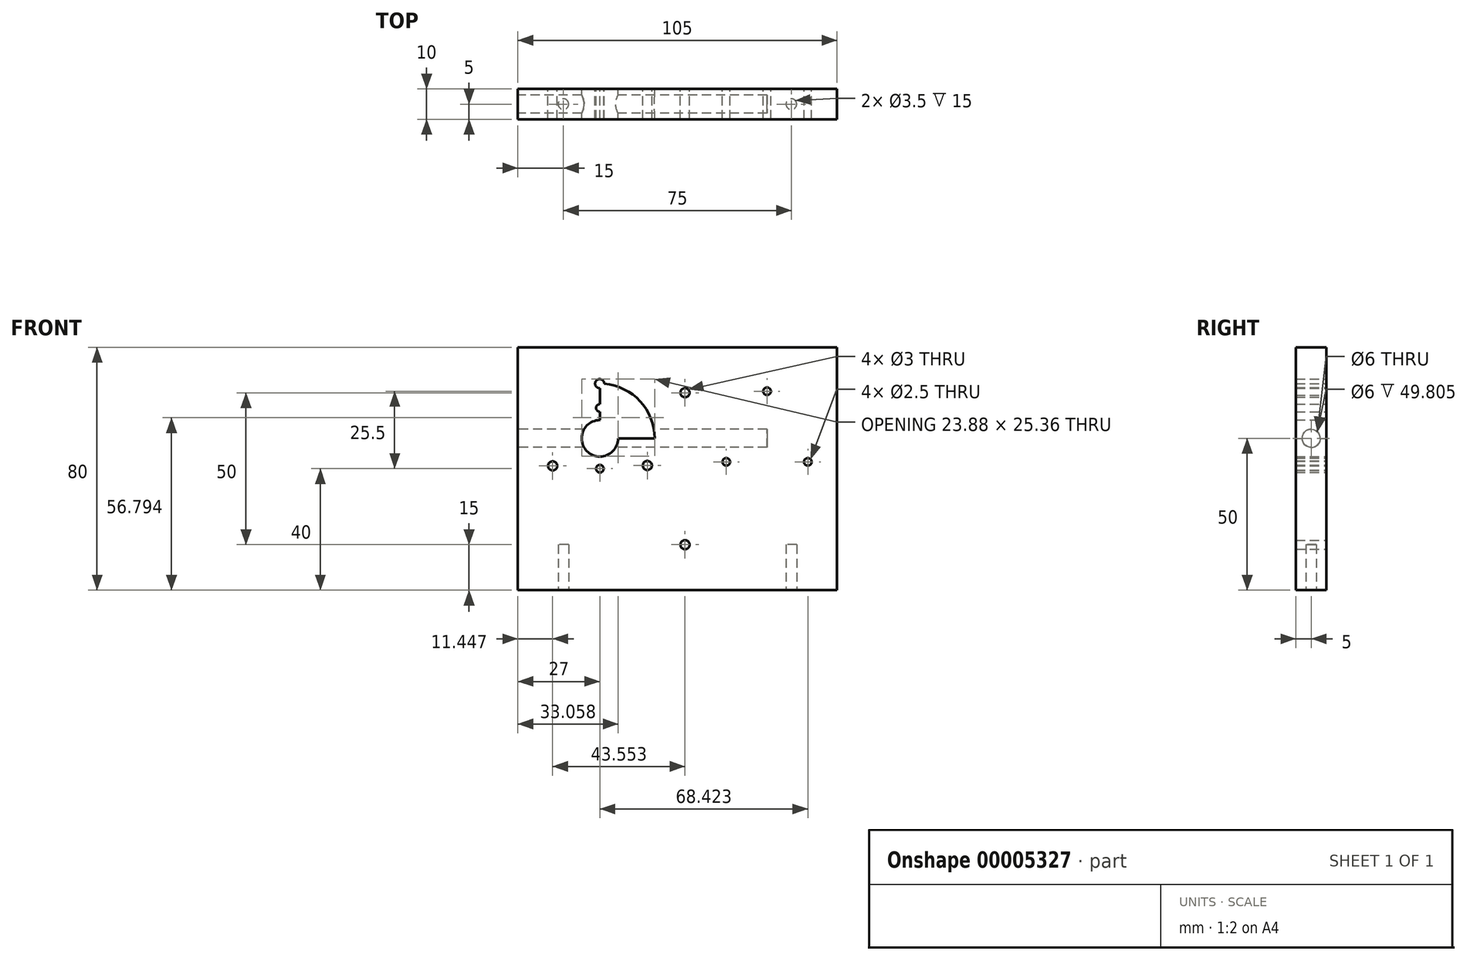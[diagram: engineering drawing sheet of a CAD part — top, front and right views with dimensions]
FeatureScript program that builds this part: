
annotation { "Feature Type Name" : "Feature", "Feature Type Description" : "" }
export const myFeature = defineFeature(function(context is Context, id is Id, definition is map)
    precondition{}
    {
        {
            var Q0;
            Q0=qCreatedBy(makeId("Front.planeOp"),FACE);
            var sketch = newSketch(context, id + "F0", { "sketchPlane" : qUnion([Q0])});
            skLineSegment(sketch, "E0.bottom", {"start": v(0, 0) * mm, "end": v(105, 0) * mm});
            skLineSegment(sketch, "E0.top", {"start": v(0, 80) * mm, "end": v(105, 80) * mm});
            skLineSegment(sketch, "E0.left", {"start": v(0, 0) * mm, "end": v(0, 80) * mm});
            skLineSegment(sketch, "E0.right", {"start": v(105, 0) * mm, "end": v(105, 80) * mm});
            skCircle(sketch, "E1", {"center": v(27, 50) * mm, "radius": 6 * mm});
            skCircle(sketch, "E2", {"center": v(27, 50) * mm, "radius": 18 * mm});
            skCircle(sketch, "E3", {"center": v(26.93, 68) * mm, "radius": 1.5 * mm});
            skCircle(sketch, "E4.1.0", {"center": v(11.45, 40.94) * mm, "radius": 1.5 * mm});
            skCircle(sketch, "E4.2.0", {"center": v(42.62, 41.06) * mm, "radius": 1.5 * mm});
            skLineSegment(sketch, "E5", {"start": v(27, 50) * mm, "end": v(27, 85.98) * mm});
            skLineSegment(sketch, "E6", {"start": v(27, 85.98) * mm, "end": v(27, 10.6) * mm});
            skCircle(sketch, "E7", {"center": v(27, 60) * mm, "radius": 1.25 * mm});
            skCircle(sketch, "E8", {"center": v(27, 40) * mm, "radius": 1.25 * mm});
            skLineSegment(sketch, "E9", {"start": v(27, 50) * mm, "end": v(101.77, 50) * mm});
            skCircle(sketch, "E10", {"center": v(82, 50) * mm, "radius": 15.5 * mm});
            skLineSegment(sketch, "E11", {"start": v(82, 50) * mm, "end": v(82, 71.42) * mm});
            skCircle(sketch, "E12", {"center": v(82, 65.5) * mm, "radius": 1.25 * mm});
            skCircle(sketch, "E13.1.0", {"center": v(95.42, 42.25) * mm, "radius": 1.25 * mm});
            skCircle(sketch, "E13.2.0", {"center": v(68.58, 42.25) * mm, "radius": 1.25 * mm});
            skLineSegment(sketch, "E13.anchor1", {"start": v(82, 50) * mm, "end": v(82, 65.5) * mm, "construction": true});
            skLineSegment(sketch, "E13.anchor2", {"start": v(82, 50) * mm, "end": v(68.58, 42.25) * mm, "construction": true});
            skCircle(sketch, "E14", {"center": v(55, 65) * mm, "radius": 1.5 * mm});
            skLineSegment(sketch, "E15", {"start": v(55, 65) * mm, "end": v(55, 3.51) * mm});
            skCircle(sketch, "E16", {"center": v(55, 15) * mm, "radius": 1.5 * mm});
            skSolve(sketch);
        }
        {
            var Q0;
            Q0=makeQuery(id+"F0.imprint","IMPRINT",FACE,{"disambiguationData":[TD([[makeQuery(id+"F0.imprint","IMPRINT",EDGE,{"derivedFrom":sQuery(id+"F0.wireOp",EDGE,"E0.bottom")}),1.0]])]});
            var Q1;
            {var subQ1=sQuery(id+"F0.wireOp",EDGE,"E6");var subQ4=sQuery(id+"F0.wireOp",EDGE,"E1");var subQ9=makeQuery(id+"F0.imprint","INTERSECT",VERTEX,{"disambiguationData":[OD(0.0)],"derivedFrom":[subQ4,subQ1]});Q1=makeQuery(id+"F0.imprint","IMPRINT",FACE,{"disambiguationData":[TD([[makeQuery(id+"F0.imprint","IMPRINT",EDGE,{"disambiguationData":[TD([[subQ9,-1.0]])],"derivedFrom":subQ4}),-1.0]])]});}
            var Q2;
            {var subQ1=sQuery(id+"F0.wireOp",EDGE,"E1");var subQ6=sQuery(id+"F0.wireOp",EDGE,"E6");var subQ9=makeQuery(id+"F0.imprint","INTERSECT",VERTEX,{"disambiguationData":[OD(0.0)],"derivedFrom":[subQ1,subQ6]});Q2=makeQuery(id+"F0.imprint","IMPRINT",FACE,{"disambiguationData":[TD([[makeQuery(id+"F0.imprint","IMPRINT",EDGE,{"disambiguationData":[TD([[subQ9,1.0]])],"derivedFrom":subQ1}),-1.0]])]});}
            var Q3;
            {var subQ6=sQuery(id+"F0.wireOp",EDGE,"E9");var subQ7=sQuery(id+"F0.wireOp",EDGE,"E1");var subQ8=makeQuery(id+"F0.imprint","INTERSECT",VERTEX,{"derivedFrom":[subQ7,subQ6]});Q3=makeQuery(id+"F0.imprint","IMPRINT",FACE,{"disambiguationData":[TD([[makeQuery(id+"F0.imprint","IMPRINT",EDGE,{"disambiguationData":[TD([[subQ8,1.0]])],"derivedFrom":subQ7}),-1.0]])]});}
            var Q4;
            {var subQ7=sQuery(id+"F0.wireOp",EDGE,"E9");var subQ9=makeQuery(id+"F0.imprint","INTERSECT",VERTEX,{"derivedFrom":[subQ7,sQuery(id+"F0.wireOp",EDGE,"E11")]});Q4=makeQuery(id+"F0.imprint","IMPRINT",FACE,{"disambiguationData":[TD([[makeQuery(id+"F0.imprint","IMPRINT",EDGE,{"disambiguationData":[TD([[subQ9,1.0]])],"derivedFrom":subQ7}),-1.0]])]});}
            var Q5;
            {var subQ1=sQuery(id+"F0.wireOp",EDGE,"E11");var subQ5=sQuery(id+"F0.wireOp",EDGE,"E9");var subQ6=makeQuery(id+"F0.imprint","INTERSECT",VERTEX,{"derivedFrom":[subQ5,subQ1]});Q5=makeQuery(id+"F0.imprint","IMPRINT",FACE,{"disambiguationData":[TD([[makeQuery(id+"F0.imprint","IMPRINT",EDGE,{"disambiguationData":[TD([[subQ6,1.0]])],"derivedFrom":subQ5}),1.0]])]});}
            var Q6;
            {var subQ1=sQuery(id+"F0.wireOp",EDGE,"E11");var subQ5=sQuery(id+"F0.wireOp",EDGE,"E9");var subQ6=makeQuery(id+"F0.imprint","INTERSECT",VERTEX,{"derivedFrom":[subQ5,subQ1]});Q6=makeQuery(id+"F0.imprint","IMPRINT",FACE,{"disambiguationData":[TD([[makeQuery(id+"F0.imprint","IMPRINT",EDGE,{"disambiguationData":[TD([[subQ6,-1.0]])],"derivedFrom":subQ5}),1.0]])]});}
            extrude(context, id + "F1", {"entities" : qUnion([Q0, Q1, Q2, Q3, Q4, Q5, Q6]), "depth" : 10 * mm});
        }
        {
            var Q0;
            Q0=qCreatedBy(makeId("Right.planeOp"),FACE);
            var sketch = newSketch(context, id + "F2", { "sketchPlane" : qUnion([Q0])});
            skCircle(sketch, "E17", {"center": v(-5, 50) * mm, "radius": 3 * mm});
            skSolve(sketch);
        }
        {
            var Q0;
            Q0=makeQuery(id+"F2.imprint","IMPRINT",FACE,{"disambiguationData":[TD([[makeQuery(id+"F2.imprint","IMPRINT",EDGE,{"derivedFrom":sQuery(id+"F2.wireOp",EDGE,"E17")}),1.0]])]});
            extrude(context, id + "F3", {"entities" : qUnion([Q0]), "operationType" : NewBodyOperationType.REMOVE, "depth" : 82 * mm});
        }
        {
            var Q0;
            Q0=qCreatedBy(makeId("Top.planeOp"),FACE);
            var sketch = newSketch(context, id + "F4", { "sketchPlane" : qUnion([Q0])});
            skCircle(sketch, "E18", {"center": v(15, -5) * mm, "radius": 1.75 * mm});
            skCircle(sketch, "E19", {"center": v(90, -5) * mm, "radius": 1.75 * mm});
            skSolve(sketch);
        }
        {
            var Q0;
            Q0=makeQuery(id+"F4.imprint","IMPRINT",FACE,{"disambiguationData":[TD([[makeQuery(id+"F4.imprint","IMPRINT",EDGE,{"derivedFrom":sQuery(id+"F4.wireOp",EDGE,"E18")}),1.0]])]});
            var Q1;
            Q1=makeQuery(id+"F4.imprint","IMPRINT",FACE,{"disambiguationData":[TD([[makeQuery(id+"F4.imprint","IMPRINT",EDGE,{"derivedFrom":sQuery(id+"F4.wireOp",EDGE,"E19")}),1.0]])]});
            extrude(context, id + "F5", {"entities" : qUnion([Q0, Q1]), "operationType" : NewBodyOperationType.REMOVE, "depth" : 15 * mm});
        }
    });
